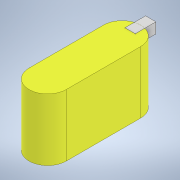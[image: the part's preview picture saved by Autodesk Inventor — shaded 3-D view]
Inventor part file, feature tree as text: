
AUTODESK INVENTOR PART (.ipt)
format: ipt  version: 2020 (Build 240168000, 168)  size: 114,176 bytes
history: native  units: mm
features: extrude x2, sketch x2
ambient origin geometry x8: Origin, YZ Plane, XZ Plane, XY Plane, X Axis, Y Axis, Z Axis, Center Point
bodies: Solid1 (feature_tree), Solid2 (feature_tree)
feature tree (4):
  extrude  "Extrusion1"  Depth=18.0mm
  extrude  "Extrusion2"  Depth=5.0mm
  sketch  "Sketch1"  dims[d0=54.0mm d1=18.0mm]
  sketch  "Sketch2"  dims[d2=30.0mm d3=0.0mm d4=5.0mm d5=10.0mm d6=5.0mm d7=0.1mm d8=0.0mm d9=5.0mm d10=0.0mm]
